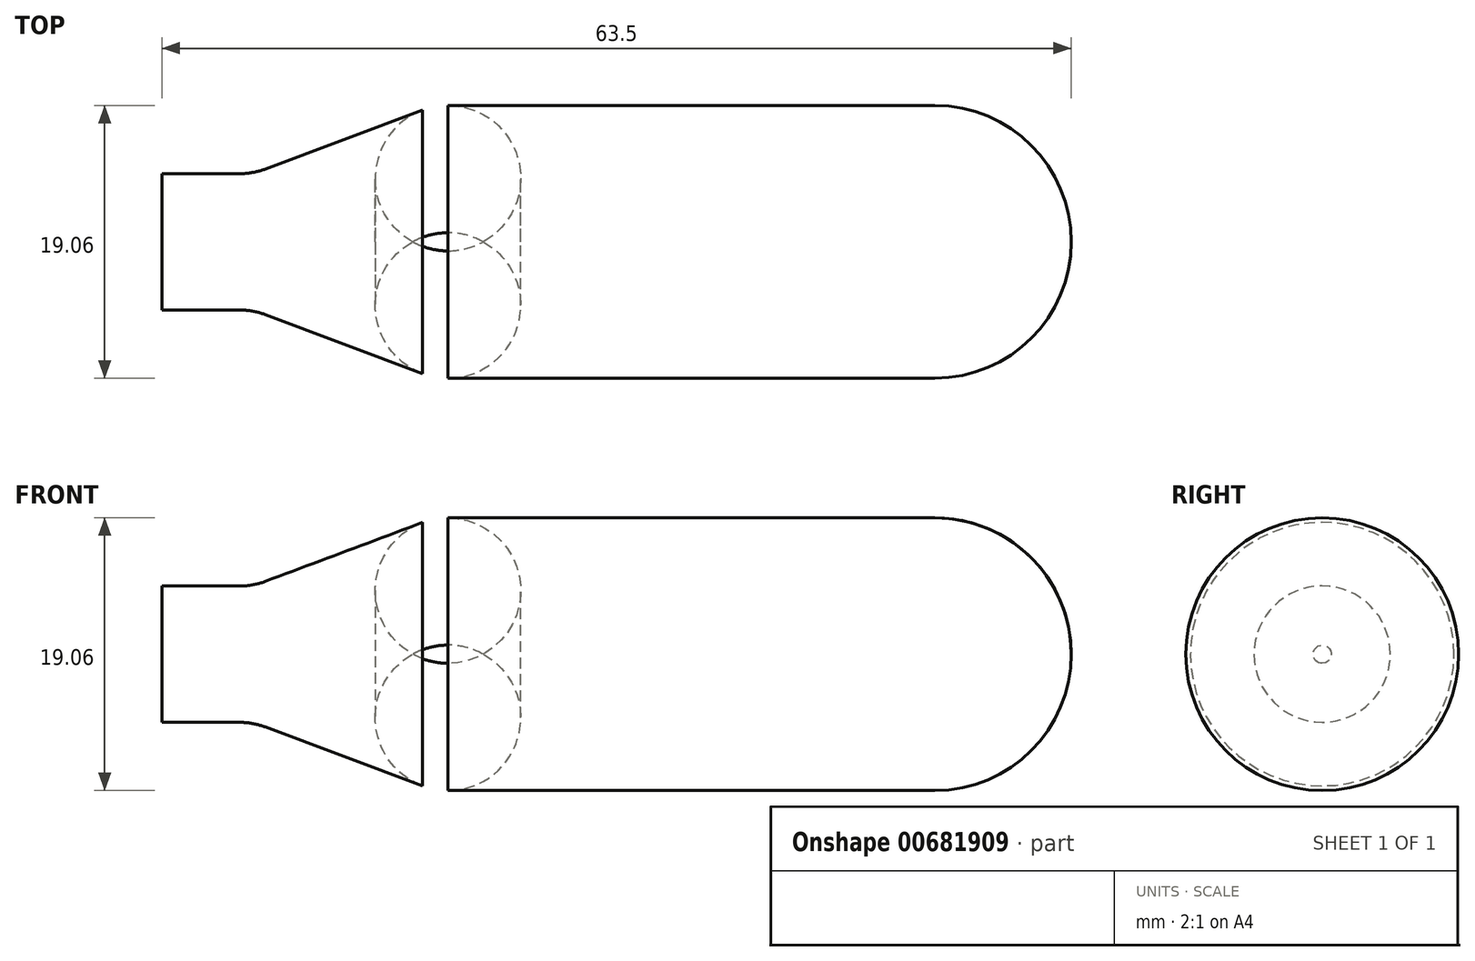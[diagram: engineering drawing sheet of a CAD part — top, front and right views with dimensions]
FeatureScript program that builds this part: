
annotation { "Feature Type Name" : "Feature", "Feature Type Description" : "" }
export const myFeature = defineFeature(function(context is Context, id is Id, definition is map)
    precondition{}
    {
        {
            var Q0;
            Q0=qCreatedBy(makeId("Front.planeOp"),FACE);
            var sketch = newSketch(context, id + "F0", { "sketchPlane" : qUnion([Q0])});
            skLineSegment(sketch, "E0", {"start": v(0, 0) * mm, "end": v(63.5, 0) * mm});
            skLineSegment(sketch, "E1", {"start": v(63.5, 0) * mm, "end": v(63.5, 9.53) * mm});
            skLineSegment(sketch, "E2", {"start": v(0, 0) * mm, "end": v(0, 4.76) * mm});
            skLineSegment(sketch, "E3", {"start": v(0, 4.76) * mm, "end": v(4.6, 4.76) * mm});
            skPoint(sketch, "E4", {"position": v(19.05, 9.53) * mm});
            skLineSegment(sketch, "E5", {"start": v(63.5, 9.53) * mm, "end": v(19.05, 9.53) * mm});
            skLineSegment(sketch, "E6", {"start": v(0, 4.76) * mm, "end": v(6.35, 4.76) * mm});
            skLineSegment(sketch, "E7", {"start": v(19.05, 9.53) * mm, "end": v(6.35, 4.76) * mm});
            skSolve(sketch);
        }
        {
            var Q0;
            Q0=makeQuery(id+"F0.imprint","IMPRINT",FACE,{"disambiguationData":[TD([[makeQuery(id+"F0.imprint","IMPRINT",EDGE,{"derivedFrom":sQuery(id+"F0.wireOp",EDGE,"E0")}),1.0]])]});
            var Q1;
            Q1=sQuery(id+"F0.wireOp",EDGE,"E0");
            revolve(context, id + "F1", {"entities" : qUnion([Q0]), "axis" : qUnion([Q1]), "revolveType" : RevolveType.FULL});
        }
        {
            var Q0;
            Q0=makeQuery(id+"F1.opRevolve","SWEPT_EDGE",EDGE,{"disambiguationData":[OSD([sQuery(id+"F0.wireOp",EDGE,"E1"),sQuery(id+"F0.wireOp",EDGE,"E5")])]});
            fillet(context, id + "F2", {"entities" : qUnion([Q0]), "radius" : 9.52 * mm, "tangentPropagation" : true, "defaultsChanged" : false, "vertexSettings" : [], "allowEdgeOverflow" : false});
        }
        {
            var Q0;
            Q0=makeQuery(id+"F1.opRevolve","SWEPT_EDGE",EDGE,{"disambiguationData":[OSD([sQuery(id+"F0.wireOp",EDGE,"E5"),sQuery(id+"F0.wireOp",EDGE,"IhDfeMiR-hXfk-T97q-Z23S-zCNNGqkhDiH1")])]});
            fillet(context, id + "F3", {"entities" : qUnion([Q0]), "radius" : 5.08 * mm, "tangentPropagation" : true, "defaultsChanged" : false, "vertexSettings" : [], "allowEdgeOverflow" : false});
        }
        {
            var Q0;
            Q0=makeQuery(id+"F1.opRevolve","SWEPT_EDGE",EDGE,{"disambiguationData":[OSD([sQuery(id+"F0.wireOp",EDGE,"E6"),sQuery(id+"F0.wireOp",EDGE,"E7")])]});
            fillet(context, id + "F4", {"entities" : qUnion([Q0]), "radius" : 5.08 * mm, "tangentPropagation" : true, "defaultsChanged" : false, "vertexSettings" : [], "allowEdgeOverflow" : false});
        }
    });
